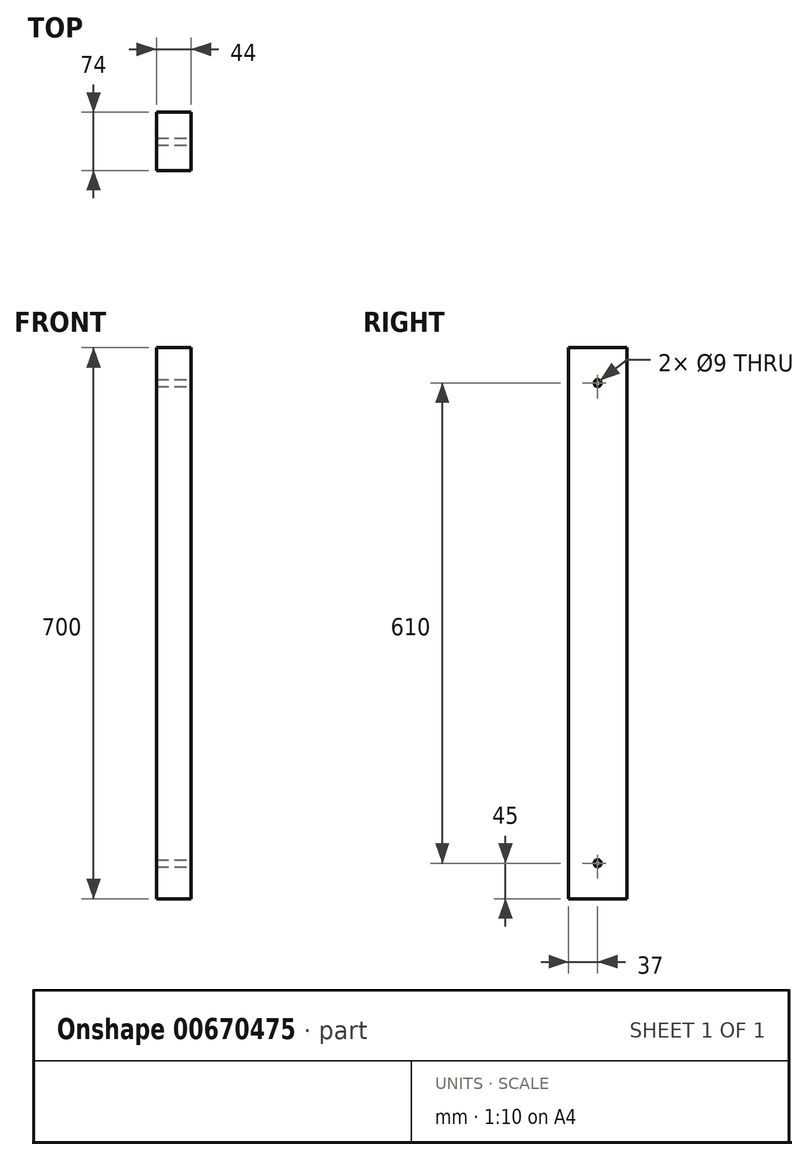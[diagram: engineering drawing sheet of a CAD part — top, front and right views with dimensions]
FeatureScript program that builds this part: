
annotation { "Feature Type Name" : "Feature", "Feature Type Description" : "" }
export const myFeature = defineFeature(function(context is Context, id is Id, definition is map)
    precondition{}
    {
        {
            var Q0;
            Q0=qCreatedBy(makeId("Top.planeOp"),FACE);
            var sketch = newSketch(context, id + "F0", { "sketchPlane" : qUnion([Q0])});
            skLineSegment(sketch, "E0.bottom", {"start": v(22, -37) * mm, "end": v(-22, -37) * mm});
            skLineSegment(sketch, "E0.top", {"start": v(22, 37) * mm, "end": v(-22, 37) * mm});
            skLineSegment(sketch, "E0.left", {"start": v(22, -37) * mm, "end": v(22, 37) * mm});
            skLineSegment(sketch, "E0.right", {"start": v(-22, -37) * mm, "end": v(-22, 37) * mm});
            skPoint(sketch, "E0.middle", {"position": v(0, 0) * mm});
            skSolve(sketch);
        }
        {
            var Q0;
            Q0=qSketchRegion(id+"F0",true);
            extrude(context, id + "F1", {"entities" : qUnion([Q0]), "depth" : 700 * mm, "offsetDistance" : 25.4 * mm});
        }
        {
            var Q0;
            Q0=makeQuery(id+"F1.opExtrude","SWEPT_FACE",FACE,{"disambiguationData":[OSD([sQuery(id+"F0.wireOp",EDGE,"E0.left")])]});
            var sketch = newSketch(context, id + "F2", { "sketchPlane" : qUnion([Q0])});
            skCircle(sketch, "E1", {"center": v(0, 655) * mm, "radius": 4.5 * mm});
            skCircle(sketch, "E2", {"center": v(0, 45) * mm, "radius": 4.5 * mm});
            skSolve(sketch);
        }
        {
            var Q0;
            Q0 = qSketchRegion(id + "F2", true);
            extrude(context, id + "F3", {"entities" : qUnion([Q0]), "operationType" : NewBodyOperationType.REMOVE, "endBound" : BoundingType.THROUGH_ALL, "oppositeDirection" : true, "depth" : 25.4 * mm, "offsetDistance" : 25.4 * mm});
        }
    });
